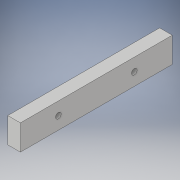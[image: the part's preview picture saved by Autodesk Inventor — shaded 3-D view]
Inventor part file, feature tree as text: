
AUTODESK INVENTOR PART (.ipt)
format: ipt  version: 2019 (Build 230136000, 136)  size: 104,960 bytes
history: native  units: in
note: dims shown in document units (in); Inventor stores cm internally (conversion verified against a paired STEP export)
features: sketch x2, extrude x1, hole x1
ambient origin geometry x8: Origin, YZ Plane, XZ Plane, XY Plane, X Axis, Y Axis, Z Axis, Center Point
bodies: Solid1 (feature_tree)
feature tree (4):
  extrude  "Extrusion1"  Depth=2.0in
  hole  "Hole1"  [1 undecoded]
  sketch  "Sketch2"  dims[d0=0.5in d1=2.0in]
  sketch  "Sketch3"  dims[d2=12.0in d3=0.0in d4=3.0in d5=3.0in d6=0.266in d7=0.75in d8=0.438in d9=1.35in d10=0.5635in d11=1.0in d12=0.8108in]
note: 1 required parameter value undecoded (feature->parameter linkage not recoverable at this tier; creation-order binding heuristic only, values carry confidence <= 0.55)
